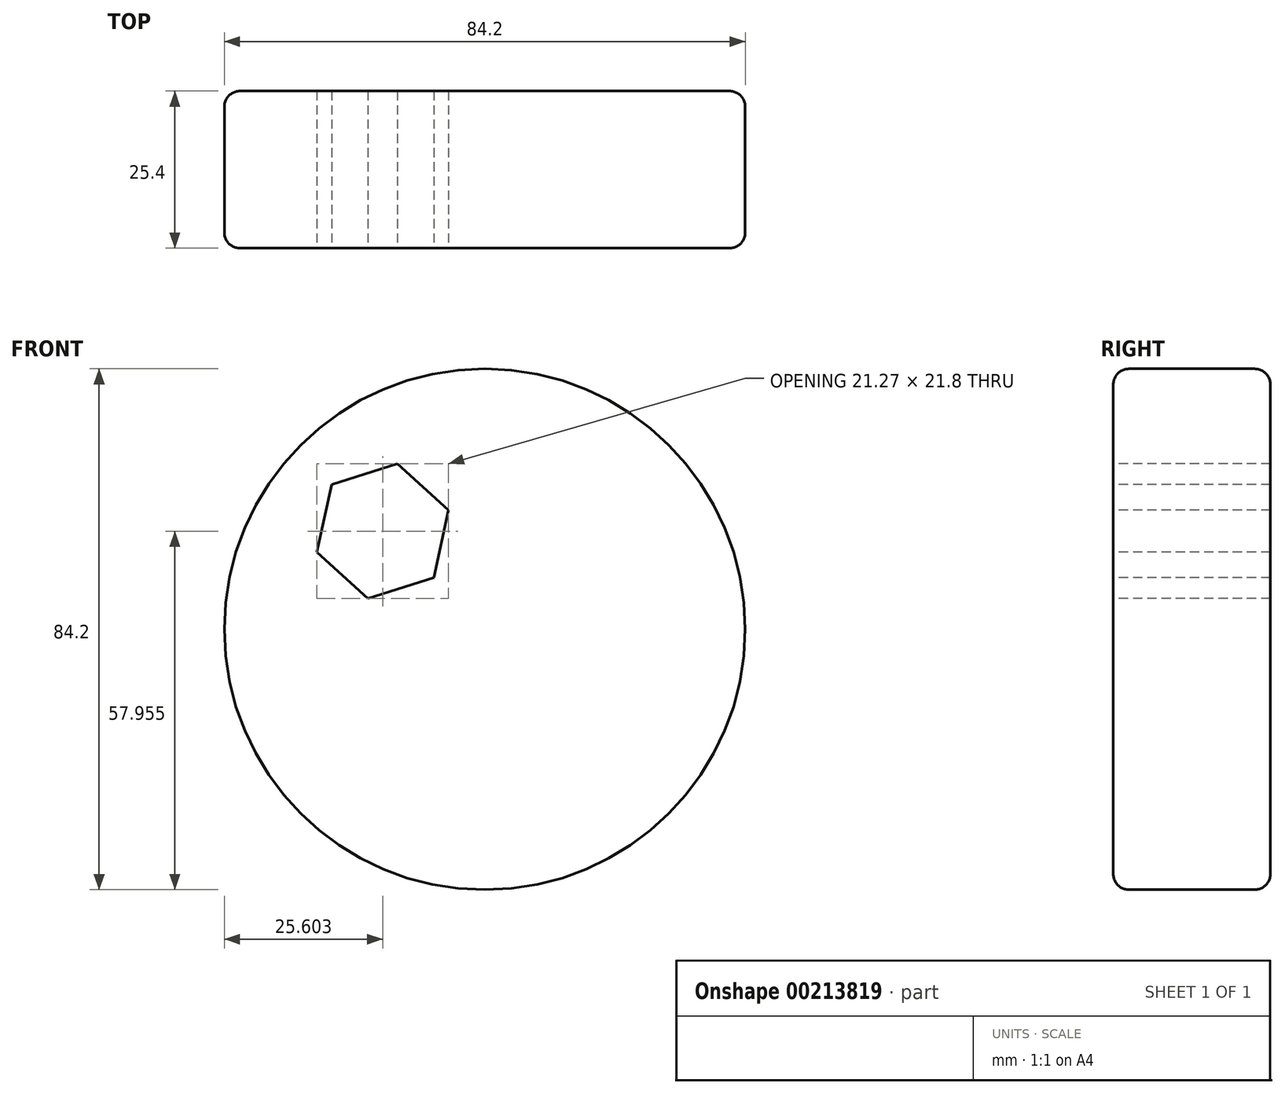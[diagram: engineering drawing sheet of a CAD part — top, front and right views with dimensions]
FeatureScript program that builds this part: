
annotation { "Feature Type Name" : "Feature", "Feature Type Description" : "" }
export const myFeature = defineFeature(function(context is Context, id is Id, definition is map)
    precondition{}
    {
        {
            var Q0;
            Q0=qCreatedBy(makeId("Front.planeOp"),FACE);
            var sketch = newSketch(context, id + "F0", { "sketchPlane" : qUnion([Q0])});
            skCircle(sketch, "E0", {"center": v(0, 0) * mm, "radius": 42.1 * mm});
            skSolve(sketch);
        }
        {
            var Q0;
            Q0=makeQuery(id+"F0.imprint","IMPRINT",FACE,{"disambiguationData":[TD([[makeQuery(id+"F0.imprint","IMPRINT",EDGE,{"derivedFrom":sQuery(id+"F0.wireOp",EDGE,"E0")}),1.0]])]});
            extrude(context, id + "F1", {"entities" : qUnion([Q0]), "depth" : 25.4 * mm});
        }
        {
            var Q0;
            Q0=makeQuery(id+"F1.opExtrude","CAP_FACE",FACE,{"disambiguationData":[OSD([sQuery(id+"F0.wireOp",EDGE,"E0")])],"isStart":false});
            var sketch = newSketch(context, id + "F2", { "sketchPlane" : qUnion([Q0])});
            skCircle(sketch, "E1.cCircle", {"center": v(-16.5, 15.86) * mm, "radius": 11.16 * mm, "construction": true});
            skLineSegment(sketch, "E1.0", {"start": v(-8.25, 8.34) * mm, "end": v(-18.88, 4.95) * mm});
            skLineSegment(sketch, "E1.1", {"start": v(-18.88, 4.95) * mm, "end": v(-27.13, 12.47) * mm});
            skLineSegment(sketch, "E1.2", {"start": v(-27.13, 12.47) * mm, "end": v(-24.75, 23.37) * mm});
            skLineSegment(sketch, "E1.3", {"start": v(-24.75, 23.37) * mm, "end": v(-14.11, 26.76) * mm});
            skLineSegment(sketch, "E1.4", {"start": v(-14.11, 26.76) * mm, "end": v(-5.86, 19.24) * mm});
            skLineSegment(sketch, "E1.5", {"start": v(-5.86, 19.24) * mm, "end": v(-8.25, 8.34) * mm});
            skSolve(sketch);
        }
        {
            var Q0;
            Q0=makeQuery(id+"F2.imprint","IMPRINT",FACE,{"disambiguationData":[TD([[makeQuery(id+"F2.imprint","IMPRINT",EDGE,{"derivedFrom":sQuery(id+"F2.wireOp",EDGE,"E1.0")}),-1.0]])]});
            extrude(context, id + "F3", {"entities" : qUnion([Q0]), "operationType" : NewBodyOperationType.REMOVE, "endBound" : BoundingType.THROUGH_ALL, "oppositeDirection" : true, "depth" : 25.4 * mm});
        }
        {
            var Q0;
            Q0=makeQuery(id+"F1.opExtrude","CAP_EDGE",EDGE,{"disambiguationData":[OSD([sQuery(id+"F0.wireOp",EDGE,"E0")])],"isStart":false});
            fillet(context, id + "F4", {"entities" : qUnion([Q0]), "radius" : 2.54 * mm, "tangentPropagation" : true, "allowEdgeOverflow" : false});
        }
        {
            var Q0;
            Q0=makeQuery(id+"F1.opExtrude","CAP_EDGE",EDGE,{"disambiguationData":[OSD([sQuery(id+"F0.wireOp",EDGE,"E0")])],"isStart":true});
            fillet(context, id + "F5", {"entities" : qUnion([Q0]), "radius" : 2.54 * mm, "tangentPropagation" : true, "allowEdgeOverflow" : false});
        }
    });
